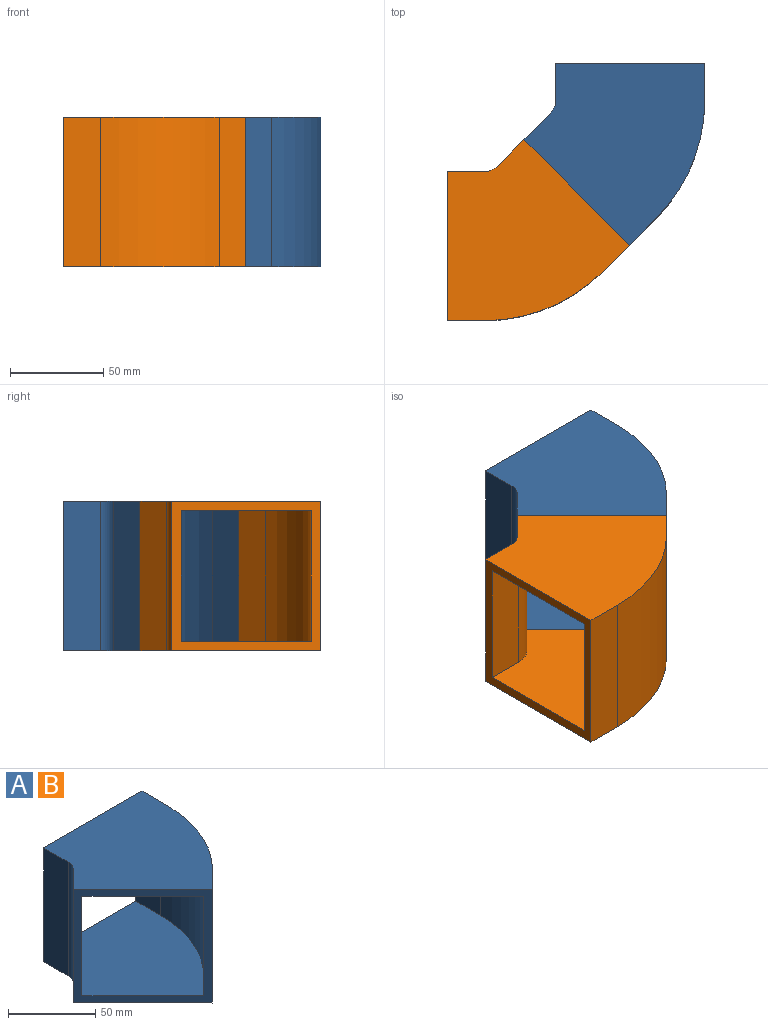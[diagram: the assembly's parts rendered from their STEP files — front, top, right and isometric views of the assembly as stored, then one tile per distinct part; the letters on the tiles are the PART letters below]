
ASSEMBLY  parts=2 mates=1
PART A: 18 faces, bbox 97.1x97.8x80 mm
  f0: plane 80x80mm, normal (0,1,0), area 1500mm2, adj f2,f3,f6,f7,f10,f14,f16,f17
  f1: plane 80x56.57mm, normal (-0.71,-0.71,0), area 1500mm2, adj f2,f3,f4,f9,f11,f15,f16,f17
  f2: plane 94.25x88.54mm, normal (0,0,1), area 5548.9mm2, adj f0,f1,f4,f5,f6,f10,f11,f12
  f3: plane 97.78x97.07mm, normal (0,0,-1), area 6341.6mm2, adj f0,f1,f7,f8,f9,f13,f14,f15
  f4: plane 70x14.14mm, normal (0.71,-0.71,0), area 1400mm2, adj f1,f2,f5,f16
  f5: cylinder r=15mm len=70mm, axis (0,0,-1), area 824.7mm2, adj f2,f4,f6,f16
  f6: plane 70x20mm, normal (1,0,0), area 1400mm2, adj f0,f2,f5,f16
  f7: plane 80x20mm, normal (-1,0,0), area 1600mm2, adj f0,f3,f8,f17
  f8: cylinder r=10mm len=80mm, axis (0,0,-1), area 628.3mm2, adj f3,f7,f9,f17
  f9: plane 80x14.14mm, normal (-0.71,0.71,0), area 1600mm2, adj f1,f3,f8,f17
  f10: plane 70x20mm, normal (-1,0,0), area 1400mm2, adj f0,f2,f12,f16
  f11: plane 70x14.14mm, normal (-0.71,0.71,0), area 1400mm2, adj f1,f2,f12,f16
  f12: cylinder r=85mm len=70mm, axis (0,0,-1), area 4673.1mm2, adj f2,f10,f11,f16
  f13: cylinder r=90mm len=80mm, axis (0,0,-1), area 5654.9mm2, adj f3,f14,f15,f17
  f14: plane 80x20mm, normal (1,0,0), area 1600mm2, adj f0,f3,f13,f17
  f15: plane 80x14.14mm, normal (0.71,-0.71,0), area 1600mm2, adj f1,f3,f13,f17
  f16: plane 94.25x88.54mm, normal (0,0,-1), area 5548.9mm2, adj f0,f1,f4,f5,f6,f10,f11,f12
  f17: plane 97.78x97.07mm, normal (0,0,1), area 6341.6mm2, adj f0,f1,f7,f8,f9,f13,f14,f15
PART B: same geometry as A
PLACE A t=(-60.18,18.85,-38.84)mm
PLACE B rot(axis=(0,0,-1),45deg) t=(-88.47,-9.43,-38.84)mm
MATE fastened B.f0 <-> A.f1  axis (0.71,0.71,0) through (-10.69,-58.93,-38.84)mm
